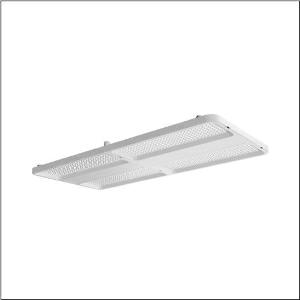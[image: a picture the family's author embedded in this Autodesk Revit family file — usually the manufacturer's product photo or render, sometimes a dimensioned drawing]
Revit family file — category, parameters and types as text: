
# Revit family: highbay_11_maxi_51hn12db4lba
name_source: partatom
category: Lighting Fixtures
units: mm (PartAtom-declared; Revit-internal decimal feet)

## family parameters
Cut with Voids When Loaded = No
Host = Face
Light Source = No
Part Type = Normal
Room Calculation Point = No
Round Connector Dimension = Use Diameter
Shared = No

## types (1)
- --- (1 x LED, 3960 lm, 19.6 W, 4000K)
    Apparent Load = 20 VA
    CIE Flux Codes = 87 98 100 100 100
    Color Rendering = 80
    Color Temperature = 4000K
    Default Elevation = 1800 mm
    Description = high bay luminaire Highbay 11 maxi; direct symmetric wide distribution, light control with lens of PMMA; UGR ≤ 19 (X = 4H | Y = 8H | S = 0.25H | reflection values 70/50/20); luminous flux: 26.000lm; light colour: 840, colour temperature: 4000K, MacAdam ≤ 2 SDCM (initial), colour rendering: CRI > 80; luminous efficacy: 207,3lm/W; rated service life: 100.000h (L95) at AT= 25°C; control: DALI 2; luminaire connection: terminal, 5-pole, max. 2.5mm² (cable entry for one cable, Ø 8.5..16mm); mains connection: 230..240V, AC/DC 0/50..60Hz; connected load: 125,4W; protection rating (complete): IP40; insulation class (complete): insulation class I (protective earthing); protection symbol: D; impact resistance: IK08; certification: CE, ENEC, VDE, UKCA; luminaire for central battery installations according to EN 60598-2-22, internal wiring halogen-free; luminaire corresponds to IFS (International Featured Standards) requirements for safety and quality in the food industry; LABS conformity tested according to VDMA 24364:2018-05; ball impact resistant only with use of appropriate mounting accessories; Suitable for use in the food industry according to the specifications of IFS-Food, HACCP and/or BRC; housing frame of high-performance plastic PA6, matt traffic white (RAL 9016); cover of PMMA; dimension (LxWxH): 946 x 442 x 72mm; permissible operating ambient temperature: -40..+65°C (reducing of maximum allowable ambient temperature of 5°C with ceiling mounting); packaging unit: 1 piece; (delivery without accessories; please order mounting accessories separately)
    Height = 72 mm  [stored 0.23622 ft]
    Lamp = 1 x LED
    Lamp Light Flux = 3960 lm
    Lamp Power = 19.6 W
    Lamp count = 1
    Length = 946 mm
    Luminous efficacy = 202 lm/W
    Manufacturer = Siteco
    ModVariant = No
    Model = 51HN12DB4LBA
    Mounting Place = Ceiling
    Mounting Type = Pendant
    Number of Poles = 1
    OnlyDefault = Yes
    Power Factor = 1
    Product Name = Highbay 11 maxi
    Product group = high bay luminaire
    ProductGroupID = 902
    Protection Class = Protection class I
    Protection Degree = IP 40
    RLX_Detail_Level = 1
    RLX_Emergency_Light_Flux = 0 lm
    RLX_Emergency_Type = 0
    RLX_Emergency_Type_DB = No
    RlxData = <blob elided: 127269 chars, md5=8f6fd64e>
    Socket = socket
    Standby Power = 0 W
    System Light Flux = 3960 lm
    System Power = 20 W
    Type Comments = : DC mode (central or group accumulator) initial emergency light level
    Type Image = l_1376023.jpg
    URL = http://relux.com
    VarID = @adj_016327
    Voltage = 0 V
    Weight = 0.00 kg
    Width = 442 mm

note: [stored X ft] marks values corroborated as IEEE doubles in the binary element streams (Revit-internal decimal feet)

## geometry (parser evidence)
native form markers: Blend x4, Sweep x10
no freeform markers — native parametric forms only
